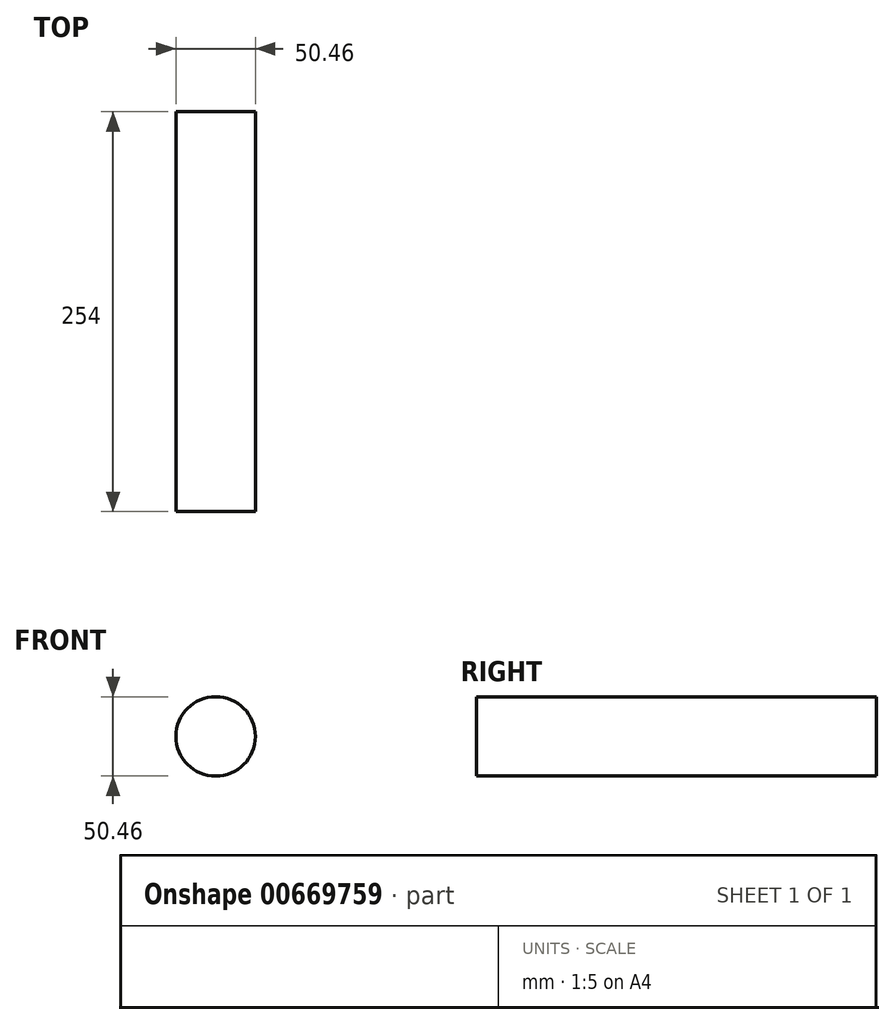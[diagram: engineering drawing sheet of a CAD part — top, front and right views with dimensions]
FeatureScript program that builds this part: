
annotation { "Feature Type Name" : "Feature", "Feature Type Description" : "" }
export const myFeature = defineFeature(function(context is Context, id is Id, definition is map)
    precondition{}
    {
        {
            var Q0;
            Q0=qCreatedBy(makeId("Front.planeOp"),FACE);
            var sketch = newSketch(context, id + "F0", { "sketchPlane" : qUnion([Q0])});
            skCircle(sketch, "E0", {"center": v(0, 0) * mm, "radius": 25.23 * mm});
            skSolve(sketch);
        }
        {
            var Q0;
            Q0 = qSketchRegion(id + "F0", true);
            extrude(context, id + "F1", {"entities" : qUnion([Q0]), "depth" : 254 * mm, "offsetDistance" : 25.4 * mm});
        }
    });
